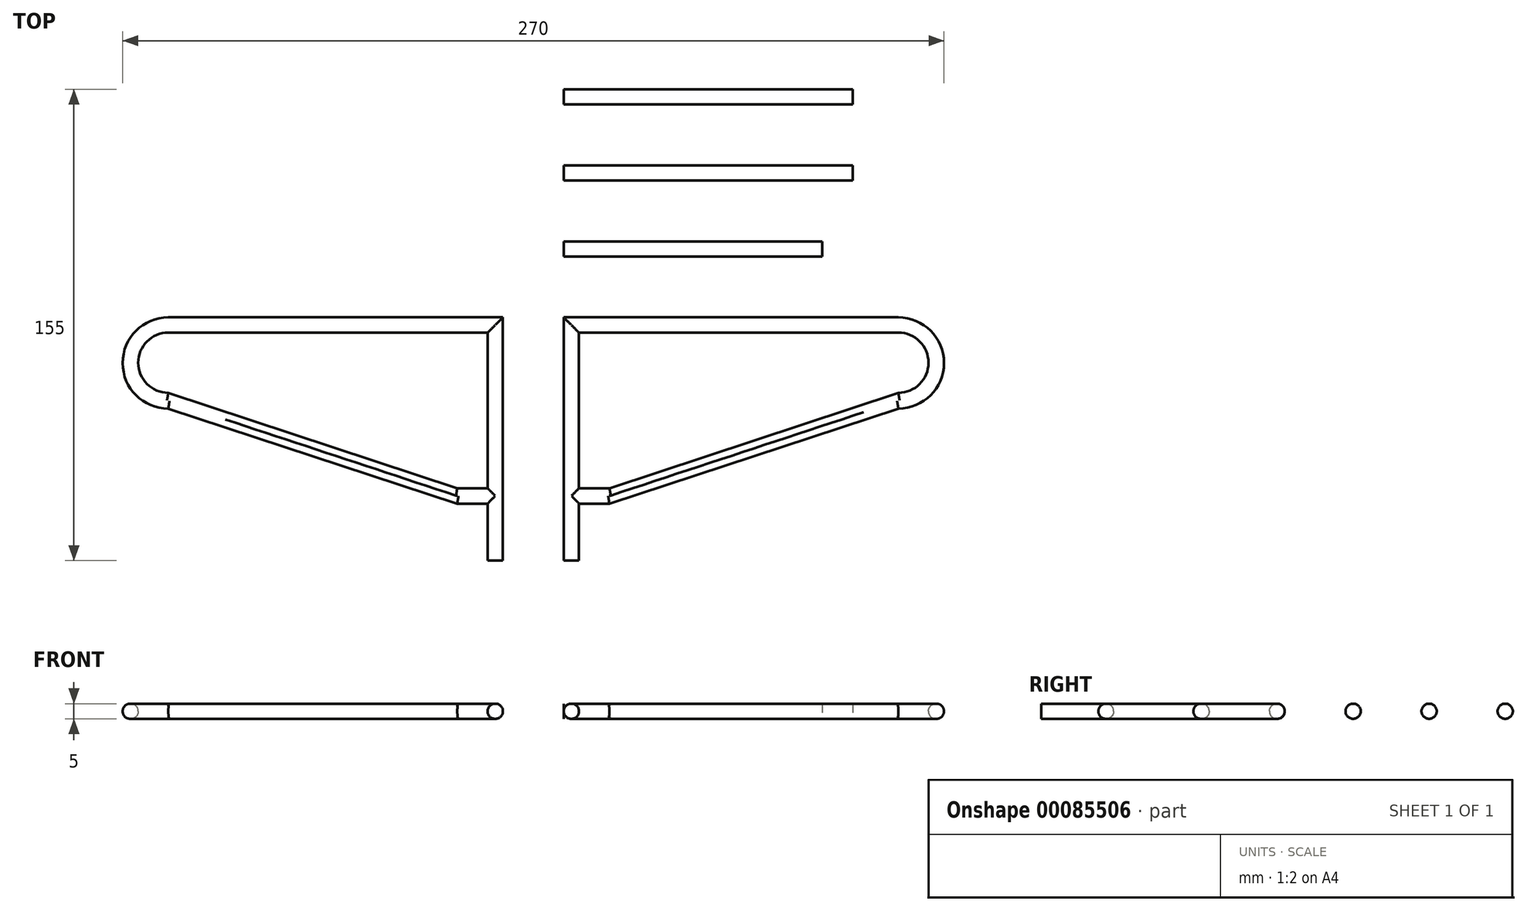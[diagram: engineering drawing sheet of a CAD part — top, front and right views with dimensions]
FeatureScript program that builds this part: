
annotation { "Feature Type Name" : "Feature", "Feature Type Description" : "" }
export const myFeature = defineFeature(function(context is Context, id is Id, definition is map)
    precondition{}
    {
        {
            var Q0;
            Q0=qCreatedBy(makeId("Top.planeOp"),FACE);
            var sketch = newSketch(context, id + "F0", { "sketchPlane" : qUnion([Q0])});
            skLineSegment(sketch, "E0", {"start": v(0, 0) * mm, "end": v(20, 0) * mm});
            skLineSegment(sketch, "E1", {"start": v(20, 0) * mm, "end": v(20, -18.78) * mm});
            skLineSegment(sketch, "E2", {"start": v(20, -18.78) * mm, "end": v(20, 61.22) * mm});
            skLineSegment(sketch, "E3", {"start": v(20, 61.22) * mm, "end": v(130, 61.22) * mm});
            skArc(sketch, "E4", {"start": v(130, 31.22) * mm, "mid": v(145, 46.22) * mm, "end": v(130, 61.22) * mm});
            skLineSegment(sketch, "E5", {"start": v(130, 31.22) * mm, "end": v(35, 0) * mm});
            skLineSegment(sketch, "E6", {"start": v(35, 0) * mm, "end": v(20, 0) * mm});
            skLineSegment(sketch, "E7", {"start": v(0, 0) * mm, "end": v(0, -18.78) * mm});
            skLineSegment(sketch, "E8", {"start": v(0, -18.78) * mm, "end": v(0, 61.22) * mm});
            skLineSegment(sketch, "E9", {"start": v(0, 61.22) * mm, "end": v(-110, 61.22) * mm});
            skArc(sketch, "E10", {"start": v(-110, 61.22) * mm, "mid": v(-125, 46.22) * mm, "end": v(-110, 31.22) * mm});
            skLineSegment(sketch, "E11", {"start": v(-110, 31.22) * mm, "end": v(-15, 0) * mm});
            skLineSegment(sketch, "E12", {"start": v(-15, 0) * mm, "end": v(0, 0) * mm});
            skLineSegment(sketch, "E13", {"start": v(-5, 5) * mm, "end": v(-5, 56.22) * mm});
            skLineSegment(sketch, "E14", {"start": v(-5, 56.22) * mm, "end": v(-110, 56.22) * mm});
            skLineSegment(sketch, "E15", {"start": v(-5, 5) * mm, "end": v(-15.01, 5) * mm});
            skLineSegment(sketch, "E16", {"start": v(-15.01, 5) * mm, "end": v(-110, 36.42) * mm});
            skArc(sketch, "E17", {"start": v(-110, 56.22) * mm, "mid": v(-119.9, 46.32) * mm, "end": v(-110, 36.42) * mm});
            skLineSegment(sketch, "E18", {"start": v(130, 56.22) * mm, "end": v(25, 56.22) * mm});
            skLineSegment(sketch, "E19", {"start": v(25, 56.22) * mm, "end": v(25, 5) * mm});
            skLineSegment(sketch, "E20", {"start": v(25, 5) * mm, "end": v(35.06, 5) * mm});
            skLineSegment(sketch, "E21", {"start": v(35.06, 5) * mm, "end": v(130, 36.4) * mm});
            skArc(sketch, "E22", {"start": v(130, 36.4) * mm, "mid": v(139.9, 46.32) * mm, "end": v(130, 56.22) * mm});
            skLineSegment(sketch, "E23", {"start": v(20, -18.78) * mm, "end": v(25, -18.78) * mm});
            skLineSegment(sketch, "E24", {"start": v(25, -18.78) * mm, "end": v(25, 0) * mm});
            skLineSegment(sketch, "E25", {"start": v(25, 0) * mm, "end": v(20, 0) * mm});
            skLineSegment(sketch, "E26", {"start": v(0, -18.78) * mm, "end": v(-5, -18.78) * mm});
            skLineSegment(sketch, "E27", {"start": v(-5, -18.78) * mm, "end": v(-5, 0) * mm});
            skLineSegment(sketch, "E28", {"start": v(-5, 0) * mm, "end": v(0, 0) * mm});
            skLineSegment(sketch, "E29", {"start": v(20, 61.22) * mm, "end": v(20, 81.22) * mm});
            skLineSegment(sketch, "E30", {"start": v(20, 81.22) * mm, "end": v(105, 81.22) * mm});
            skLineSegment(sketch, "E31", {"start": v(105, 81.22) * mm, "end": v(105, 86.22) * mm});
            skLineSegment(sketch, "E32", {"start": v(105, 86.22) * mm, "end": v(20, 86.22) * mm});
            skLineSegment(sketch, "E33", {"start": v(20, 86.22) * mm, "end": v(20, 81.22) * mm});
            skLineSegment(sketch, "E34", {"start": v(20, 86.22) * mm, "end": v(20, 106.22) * mm});
            skLineSegment(sketch, "E35", {"start": v(20, 106.22) * mm, "end": v(115, 106.22) * mm});
            skLineSegment(sketch, "E36", {"start": v(115, 106.22) * mm, "end": v(115, 111.22) * mm});
            skLineSegment(sketch, "E37", {"start": v(115, 111.22) * mm, "end": v(20, 111.22) * mm});
            skLineSegment(sketch, "E38", {"start": v(20, 111.22) * mm, "end": v(20, 106.22) * mm});
            skLineSegment(sketch, "E39", {"start": v(20, 111.22) * mm, "end": v(20, 131.22) * mm});
            skLineSegment(sketch, "E40", {"start": v(20, 131.22) * mm, "end": v(115, 131.22) * mm});
            skLineSegment(sketch, "E41", {"start": v(115, 131.22) * mm, "end": v(115, 136.22) * mm});
            skLineSegment(sketch, "E42", {"start": v(115, 136.22) * mm, "end": v(20, 136.22) * mm});
            skLineSegment(sketch, "E43", {"start": v(20, 136.22) * mm, "end": v(20, 131.22) * mm});
            skSolve(sketch);
        }
        {
            var Q0;
            Q0 = qSketchRegion(id + "F0", true);
            extrude(context, id + "F1", {"entities" : qUnion([Q0]), "depth" : 5 * mm});
        }
        {
            var Q0;
            Q0=makeQuery(id+"F1.opExtrude","CAP_EDGE",EDGE,{"disambiguationData":[OSD([sQuery(id+"F0.wireOp",EDGE,"E2")])],"isStart":true});
            var Q1;
            Q1=makeQuery(id+"F1.opExtrude","CAP_EDGE",EDGE,{"disambiguationData":[OSD([sQuery(id+"F0.wireOp",EDGE,"E19")])],"isStart":true});
            var Q2;
            Q2=makeQuery(id+"F1.opExtrude","CAP_EDGE",EDGE,{"disambiguationData":[OSD([sQuery(id+"F0.wireOp",EDGE,"E6")])],"isStart":true});
            var Q3;
            Q3=makeQuery(id+"F1.opExtrude","CAP_EDGE",EDGE,{"disambiguationData":[OSD([sQuery(id+"F0.wireOp",EDGE,"E5")])],"isStart":true});
            var Q4;
            Q4=makeQuery(id+"F1.opExtrude","CAP_EDGE",EDGE,{"disambiguationData":[OSD([sQuery(id+"F0.wireOp",EDGE,"E21")])],"isStart":true});
            var Q5;
            Q5=makeQuery(id+"F1.opExtrude","CAP_EDGE",EDGE,{"disambiguationData":[OSD([sQuery(id+"F0.wireOp",EDGE,"E20")])],"isStart":true});
            var Q6;
            Q6=makeQuery(id+"F1.opExtrude","CAP_EDGE",EDGE,{"disambiguationData":[OSD([sQuery(id+"F0.wireOp",EDGE,"E18")])],"isStart":true});
            var Q7;
            Q7=makeQuery(id+"F1.opExtrude","CAP_EDGE",EDGE,{"disambiguationData":[OSD([sQuery(id+"F0.wireOp",EDGE,"E3")])],"isStart":true});
            var Q8;
            Q8=makeQuery(id+"F1.opExtrude","CAP_EDGE",EDGE,{"disambiguationData":[OSD([sQuery(id+"F0.wireOp",EDGE,"E5")])],"isStart":false});
            var Q9;
            Q9=makeQuery(id+"F1.opExtrude","CAP_EDGE",EDGE,{"disambiguationData":[OSD([sQuery(id+"F0.wireOp",EDGE,"E6")])],"isStart":false});
            var Q10;
            Q10=makeQuery(id+"F1.opExtrude","CAP_EDGE",EDGE,{"disambiguationData":[OSD([sQuery(id+"F0.wireOp",EDGE,"E2")])],"isStart":false});
            var Q11;
            Q11=makeQuery(id+"F1.opExtrude","CAP_EDGE",EDGE,{"disambiguationData":[OSD([sQuery(id+"F0.wireOp",EDGE,"E3")])],"isStart":false});
            var Q12;
            Q12=makeQuery(id+"F1.opExtrude","CAP_EDGE",EDGE,{"disambiguationData":[OSD([sQuery(id+"F0.wireOp",EDGE,"E18")])],"isStart":false});
            var Q13;
            Q13=makeQuery(id+"F1.opExtrude","CAP_EDGE",EDGE,{"disambiguationData":[OSD([sQuery(id+"F0.wireOp",EDGE,"E19")])],"isStart":false});
            var Q14;
            Q14=makeQuery(id+"F1.opExtrude","CAP_EDGE",EDGE,{"disambiguationData":[OSD([sQuery(id+"F0.wireOp",EDGE,"E20")])],"isStart":false});
            var Q15;
            Q15=makeQuery(id+"F1.opExtrude","CAP_EDGE",EDGE,{"disambiguationData":[OSD([sQuery(id+"F0.wireOp",EDGE,"E21")])],"isStart":false});
            fillet(context, id + "F2", {"entities" : qUnion([Q0, Q1, Q2, Q3, Q4, Q5, Q6, Q7, Q8, Q9, Q10, Q11, Q12, Q13, Q14, Q15]), "radius" : 2.45 * mm, "tangentPropagation" : true, "allowEdgeOverflow" : false});
        }
        {
            var Q0;
            Q0=makeQuery(id+"F1.opExtrude","CAP_EDGE",EDGE,{"disambiguationData":[OSD([sQuery(id+"F0.wireOp",EDGE,"E8")])],"isStart":true});
            var Q1;
            Q1=makeQuery(id+"F1.opExtrude","CAP_EDGE",EDGE,{"disambiguationData":[OSD([sQuery(id+"F0.wireOp",EDGE,"E13")])],"isStart":true});
            var Q2;
            Q2=makeQuery(id+"F1.opExtrude","CAP_EDGE",EDGE,{"disambiguationData":[OSD([sQuery(id+"F0.wireOp",EDGE,"E12")])],"isStart":true});
            var Q3;
            Q3=makeQuery(id+"F1.opExtrude","CAP_EDGE",EDGE,{"disambiguationData":[OSD([sQuery(id+"F0.wireOp",EDGE,"E15")])],"isStart":true});
            var Q4;
            Q4=makeQuery(id+"F1.opExtrude","CAP_EDGE",EDGE,{"disambiguationData":[OSD([sQuery(id+"F0.wireOp",EDGE,"E14")])],"isStart":true});
            var Q5;
            Q5=makeQuery(id+"F1.opExtrude","CAP_EDGE",EDGE,{"disambiguationData":[OSD([sQuery(id+"F0.wireOp",EDGE,"E11")])],"isStart":true});
            var Q6;
            Q6=makeQuery(id+"F1.opExtrude","CAP_EDGE",EDGE,{"disambiguationData":[OSD([sQuery(id+"F0.wireOp",EDGE,"E16")])],"isStart":true});
            var Q7;
            Q7=makeQuery(id+"F1.opExtrude","CAP_EDGE",EDGE,{"disambiguationData":[OSD([sQuery(id+"F0.wireOp",EDGE,"E9")])],"isStart":true});
            var Q8;
            Q8=makeQuery(id+"F1.opExtrude","CAP_EDGE",EDGE,{"disambiguationData":[OSD([sQuery(id+"F0.wireOp",EDGE,"E11")])],"isStart":false});
            var Q9;
            Q9=makeQuery(id+"F1.opExtrude","CAP_EDGE",EDGE,{"disambiguationData":[OSD([sQuery(id+"F0.wireOp",EDGE,"E12")])],"isStart":false});
            var Q10;
            Q10=makeQuery(id+"F1.opExtrude","CAP_EDGE",EDGE,{"disambiguationData":[OSD([sQuery(id+"F0.wireOp",EDGE,"E8")])],"isStart":false});
            var Q11;
            Q11=makeQuery(id+"F1.opExtrude","CAP_EDGE",EDGE,{"disambiguationData":[OSD([sQuery(id+"F0.wireOp",EDGE,"E13")])],"isStart":false});
            var Q12;
            Q12=makeQuery(id+"F1.opExtrude","CAP_EDGE",EDGE,{"disambiguationData":[OSD([sQuery(id+"F0.wireOp",EDGE,"E14")])],"isStart":false});
            var Q13;
            Q13=makeQuery(id+"F1.opExtrude","CAP_EDGE",EDGE,{"disambiguationData":[OSD([sQuery(id+"F0.wireOp",EDGE,"E9")])],"isStart":false});
            var Q14;
            Q14=makeQuery(id+"F1.opExtrude","CAP_EDGE",EDGE,{"disambiguationData":[OSD([sQuery(id+"F0.wireOp",EDGE,"E15")])],"isStart":false});
            var Q15;
            Q15=makeQuery(id+"F1.opExtrude","CAP_EDGE",EDGE,{"disambiguationData":[OSD([sQuery(id+"F0.wireOp",EDGE,"E16")])],"isStart":false});
            fillet(context, id + "F3", {"entities" : qUnion([Q0, Q1, Q2, Q3, Q4, Q5, Q6, Q7, Q8, Q9, Q10, Q11, Q12, Q13, Q14, Q15]), "radius" : 2.45 * mm, "tangentPropagation" : true, "allowEdgeOverflow" : false});
        }
        {
            var Q0;
            Q0=makeQuery(id+"F1.opExtrude","CAP_EDGE",EDGE,{"disambiguationData":[OSD([sQuery(id+"F0.wireOp",EDGE,"E27")])],"isStart":false});
            var Q1;
            Q1=makeQuery(id+"F1.opExtrude","CAP_EDGE",EDGE,{"disambiguationData":[OSD([sQuery(id+"F0.wireOp",EDGE,"E24")])],"isStart":false});
            var Q2;
            Q2=makeQuery(id+"F1.opExtrude","CAP_EDGE",EDGE,{"disambiguationData":[OSD([sQuery(id+"F0.wireOp",EDGE,"E27")])],"isStart":true});
            var Q3;
            Q3=makeQuery(id+"F1.opExtrude","CAP_EDGE",EDGE,{"disambiguationData":[OSD([sQuery(id+"F0.wireOp",EDGE,"E24")])],"isStart":true});
            fillet(context, id + "F4", {"entities" : qUnion([Q0, Q1, Q2, Q3]), "radius" : 2.4 * mm, "tangentPropagation" : true, "allowEdgeOverflow" : false});
        }
        {
            var Q0;
            Q0=makeQuery(id+"F1.opExtrude","CAP_EDGE",EDGE,{"disambiguationData":[OSD([sQuery(id+"F0.wireOp",EDGE,"E30")])],"isStart":false});
            var Q1;
            Q1=makeQuery(id+"F1.opExtrude","CAP_EDGE",EDGE,{"disambiguationData":[OSD([sQuery(id+"F0.wireOp",EDGE,"E32")])],"isStart":false});
            var Q2;
            Q2=makeQuery(id+"F1.opExtrude","CAP_EDGE",EDGE,{"disambiguationData":[OSD([sQuery(id+"F0.wireOp",EDGE,"E35")])],"isStart":false});
            var Q3;
            Q3=makeQuery(id+"F1.opExtrude","CAP_EDGE",EDGE,{"disambiguationData":[OSD([sQuery(id+"F0.wireOp",EDGE,"E37")])],"isStart":false});
            var Q4;
            Q4=makeQuery(id+"F1.opExtrude","CAP_EDGE",EDGE,{"disambiguationData":[OSD([sQuery(id+"F0.wireOp",EDGE,"E40")])],"isStart":false});
            var Q5;
            Q5=makeQuery(id+"F1.opExtrude","CAP_EDGE",EDGE,{"disambiguationData":[OSD([sQuery(id+"F0.wireOp",EDGE,"E42")])],"isStart":false});
            var Q6;
            Q6=makeQuery(id+"F1.opExtrude","CAP_EDGE",EDGE,{"disambiguationData":[OSD([sQuery(id+"F0.wireOp",EDGE,"E30")])],"isStart":true});
            var Q7;
            Q7=makeQuery(id+"F1.opExtrude","CAP_EDGE",EDGE,{"disambiguationData":[OSD([sQuery(id+"F0.wireOp",EDGE,"E32")])],"isStart":true});
            var Q8;
            Q8=makeQuery(id+"F1.opExtrude","CAP_EDGE",EDGE,{"disambiguationData":[OSD([sQuery(id+"F0.wireOp",EDGE,"E35")])],"isStart":true});
            var Q9;
            Q9=makeQuery(id+"F1.opExtrude","CAP_EDGE",EDGE,{"disambiguationData":[OSD([sQuery(id+"F0.wireOp",EDGE,"E37")])],"isStart":true});
            var Q10;
            Q10=makeQuery(id+"F1.opExtrude","CAP_EDGE",EDGE,{"disambiguationData":[OSD([sQuery(id+"F0.wireOp",EDGE,"E40")])],"isStart":true});
            var Q11;
            Q11=makeQuery(id+"F1.opExtrude","CAP_EDGE",EDGE,{"disambiguationData":[OSD([sQuery(id+"F0.wireOp",EDGE,"E42")])],"isStart":true});
            fillet(context, id + "F5", {"entities" : qUnion([Q0, Q1, Q2, Q3, Q4, Q5, Q6, Q7, Q8, Q9, Q10, Q11]), "radius" : 2.5 * mm, "tangentPropagation" : true, "allowEdgeOverflow" : false});
        }
    });
